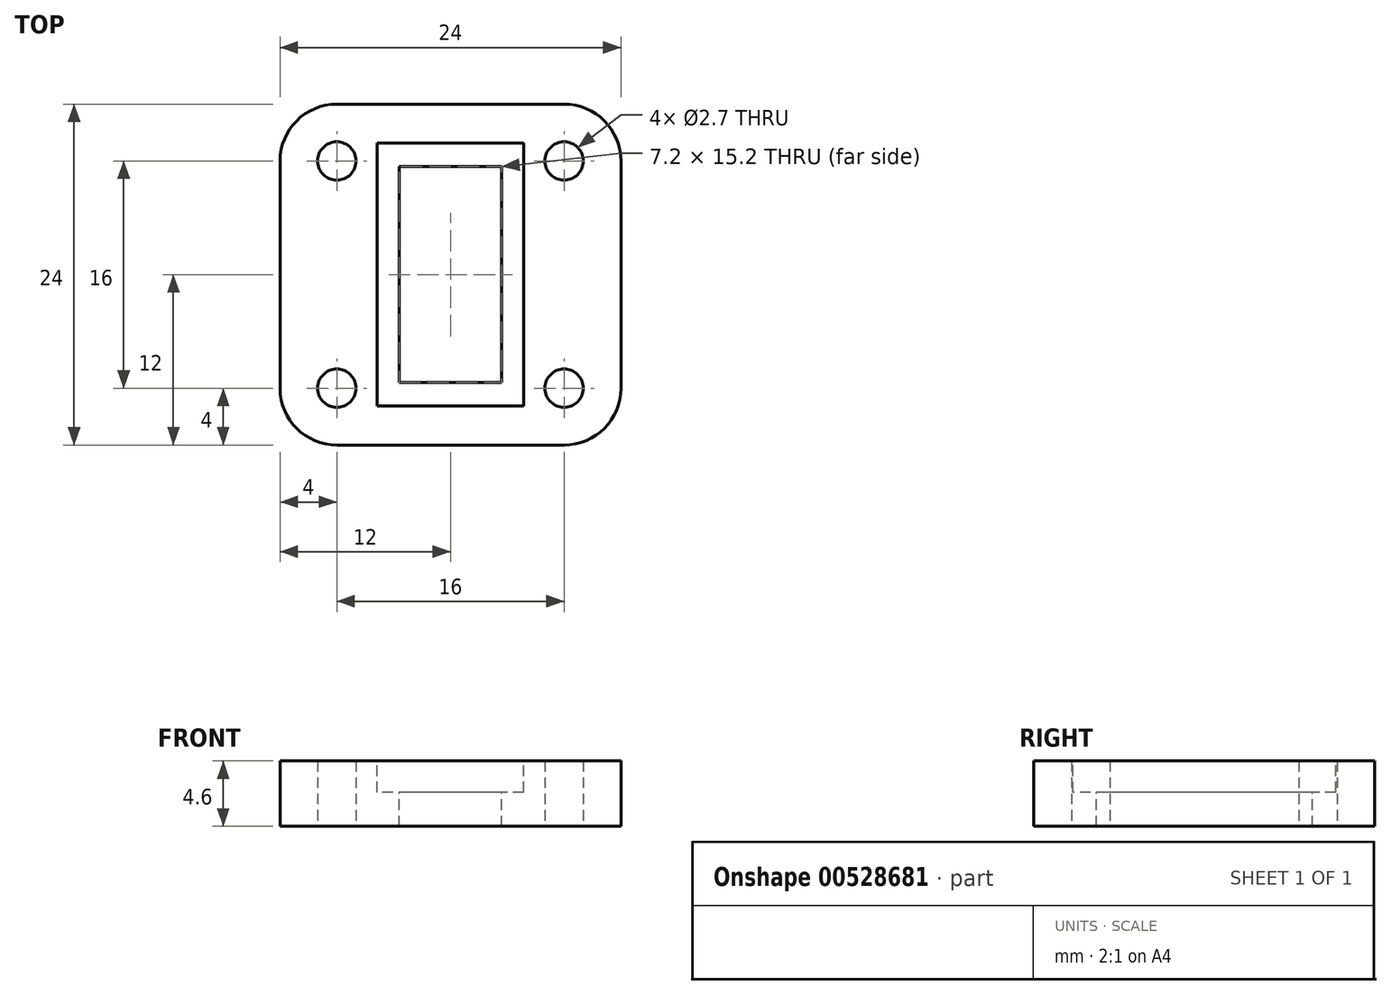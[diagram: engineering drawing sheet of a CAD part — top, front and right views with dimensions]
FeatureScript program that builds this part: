
annotation { "Feature Type Name" : "Feature", "Feature Type Description" : "" }
export const myFeature = defineFeature(function(context is Context, id is Id, definition is map)
    precondition{}
    {
        {
            var Q0;
            Q0=qCreatedBy(makeId("Top.planeOp"),FACE);
            var sketch = newSketch(context, id + "F0", { "sketchPlane" : qUnion([Q0])});
            skLineSegment(sketch, "E0.bottom", {"start": v(12, 12) * mm, "end": v(-12, 12) * mm});
            skLineSegment(sketch, "E0.top", {"start": v(12, -12) * mm, "end": v(-12, -12) * mm});
            skLineSegment(sketch, "E0.left", {"start": v(12, 12) * mm, "end": v(12, -12) * mm});
            skLineSegment(sketch, "E0.right", {"start": v(-12, 12) * mm, "end": v(-12, -12) * mm});
            skPoint(sketch, "E0.middle", {"position": v(0, 0) * mm});
            skLineSegment(sketch, "E1", {"start": v(0, 0) * mm, "end": v(-8, 0) * mm, "construction": true});
            skLineSegment(sketch, "E2", {"start": v(-8, 0) * mm, "end": v(-8, 8) * mm, "construction": true});
            skCircle(sketch, "E3", {"center": v(-8, 8) * mm, "radius": 1.35 * mm});
            skCircle(sketch, "E4.0.1.0", {"center": v(-8, -8) * mm, "radius": 1.35 * mm});
            skCircle(sketch, "E4.1.0.0", {"center": v(8, 8) * mm, "radius": 1.35 * mm});
            skCircle(sketch, "E4.1.1.0", {"center": v(8, -8) * mm, "radius": 1.35 * mm});
            skLineSegment(sketch, "E4.direction1", {"start": v(-8, 8) * mm, "end": v(8, 8) * mm, "construction": true});
            skLineSegment(sketch, "E4.direction2", {"start": v(-8, 8) * mm, "end": v(-8, -8) * mm, "construction": true});
            skSolve(sketch);
        }
        {
            var Q0;
            Q0=makeQuery(id+"F0.imprint","IMPRINT",FACE,{"disambiguationData":[TD([[makeQuery(id+"F0.imprint","IMPRINT",EDGE,{"derivedFrom":sQuery(id+"F0.wireOp",EDGE,"E0.bottom")}),1.0]])]});
            extrude(context, id + "F1", {"entities" : qUnion([Q0]), "depth" : 4.6 * mm, "offsetDistance" : 25 * mm});
        }
        {
            var Q0;
            Q0=makeQuery(id+"F1.opExtrude","CAP_FACE",FACE,{"disambiguationData":[OSD([sQuery(id+"F0.wireOp",EDGE,"E0.bottom"),sQuery(id+"F0.wireOp",EDGE,"E0.top"),sQuery(id+"F0.wireOp",EDGE,"E0.left"),sQuery(id+"F0.wireOp",EDGE,"E0.right"),sQuery(id+"F0.wireOp",EDGE,"E3"),sQuery(id+"F0.wireOp",EDGE,"0qK8BGM7-vxNI-YcJO-YgQj-w0Wkut2fyM6O"),sQuery(id+"F0.wireOp",EDGE,"E4.0.1.0"),sQuery(id+"F0.wireOp",EDGE,"E4.1.0.0"),sQuery(id+"F0.wireOp",EDGE,"E4.1.1.0"),sQuery(id+"F0.wireOp",EDGE,"8d90ac6a-7d9e-441d-8eff-2e0fc875b3620.MirrorC")])],"isStart":false});
            var sketch = newSketch(context, id + "F2", { "sketchPlane" : qUnion([Q0])});
            skLineSegment(sketch, "E5.bottom", {"start": v(3.6, 7.6) * mm, "end": v(-3.6, 7.6) * mm});
            skLineSegment(sketch, "E5.top", {"start": v(3.6, -7.6) * mm, "end": v(-3.6, -7.6) * mm});
            skLineSegment(sketch, "E5.left", {"start": v(3.6, 7.6) * mm, "end": v(3.6, -7.6) * mm});
            skLineSegment(sketch, "E5.right", {"start": v(-3.6, 7.6) * mm, "end": v(-3.6, -7.6) * mm});
            skPoint(sketch, "E5.middle", {"position": v(0, 0) * mm});
            skLineSegment(sketch, "E6.bottom", {"start": v(5.15, 9.25) * mm, "end": v(-5.15, 9.25) * mm});
            skLineSegment(sketch, "E6.top", {"start": v(5.15, -9.25) * mm, "end": v(-5.15, -9.25) * mm});
            skLineSegment(sketch, "E6.left", {"start": v(5.15, 9.25) * mm, "end": v(5.15, -9.25) * mm});
            skLineSegment(sketch, "E6.right", {"start": v(-5.15, 9.25) * mm, "end": v(-5.15, -9.25) * mm});
            skSolve(sketch);
        }
        {
            var Q0;
            Q0=makeQuery(id+"F2.imprint","IMPRINT",FACE,{"disambiguationData":[TD([[makeQuery(id+"F2.imprint","IMPRINT",EDGE,{"derivedFrom":sQuery(id+"F2.wireOp",EDGE,"E5.bottom")}),1.0]])]});
            extrude(context, id + "F3", {"entities" : qUnion([Q0]), "operationType" : NewBodyOperationType.REMOVE, "endBound" : BoundingType.THROUGH_ALL, "oppositeDirection" : true, "depth" : 5 * mm, "offsetDistance" : 25 * mm});
        }
        {
            var Q0;
            Q0 = qSketchRegion(id + "F2", true);
            extrude(context, id + "F4", {"entities" : qUnion([Q0]), "operationType" : NewBodyOperationType.REMOVE, "oppositeDirection" : true, "depth" : 2.2 * mm, "offsetDistance" : 25 * mm});
        }
        {
            var Q0;
            Q0=makeQuery(id+"F1.opExtrude","SWEPT_EDGE",EDGE,{"disambiguationData":[OSD([sQuery(id+"F0.wireOp",EDGE,"E0.bottom"),sQuery(id+"F0.wireOp",EDGE,"E0.right")])]});
            var Q1;
            Q1=makeQuery(id+"F1.opExtrude","SWEPT_EDGE",EDGE,{"disambiguationData":[OSD([sQuery(id+"F0.wireOp",EDGE,"E0.bottom"),sQuery(id+"F0.wireOp",EDGE,"E0.left")])]});
            var Q2;
            Q2=makeQuery(id+"F1.opExtrude","SWEPT_EDGE",EDGE,{"disambiguationData":[OSD([sQuery(id+"F0.wireOp",EDGE,"E0.top"),sQuery(id+"F0.wireOp",EDGE,"E0.left")])]});
            var Q3;
            Q3=makeQuery(id+"F1.opExtrude","SWEPT_EDGE",EDGE,{"disambiguationData":[OSD([sQuery(id+"F0.wireOp",EDGE,"E0.top"),sQuery(id+"F0.wireOp",EDGE,"E0.right")])]});
            fillet(context, id + "F5", {"entities" : qUnion([Q0, Q1, Q2, Q3]), "tangentPropagation" : true, "radius" : 4 * mm, "defaultsChanged" : true, "vertexSettings" : [], "allowEdgeOverflow" : false});
        }
    });
